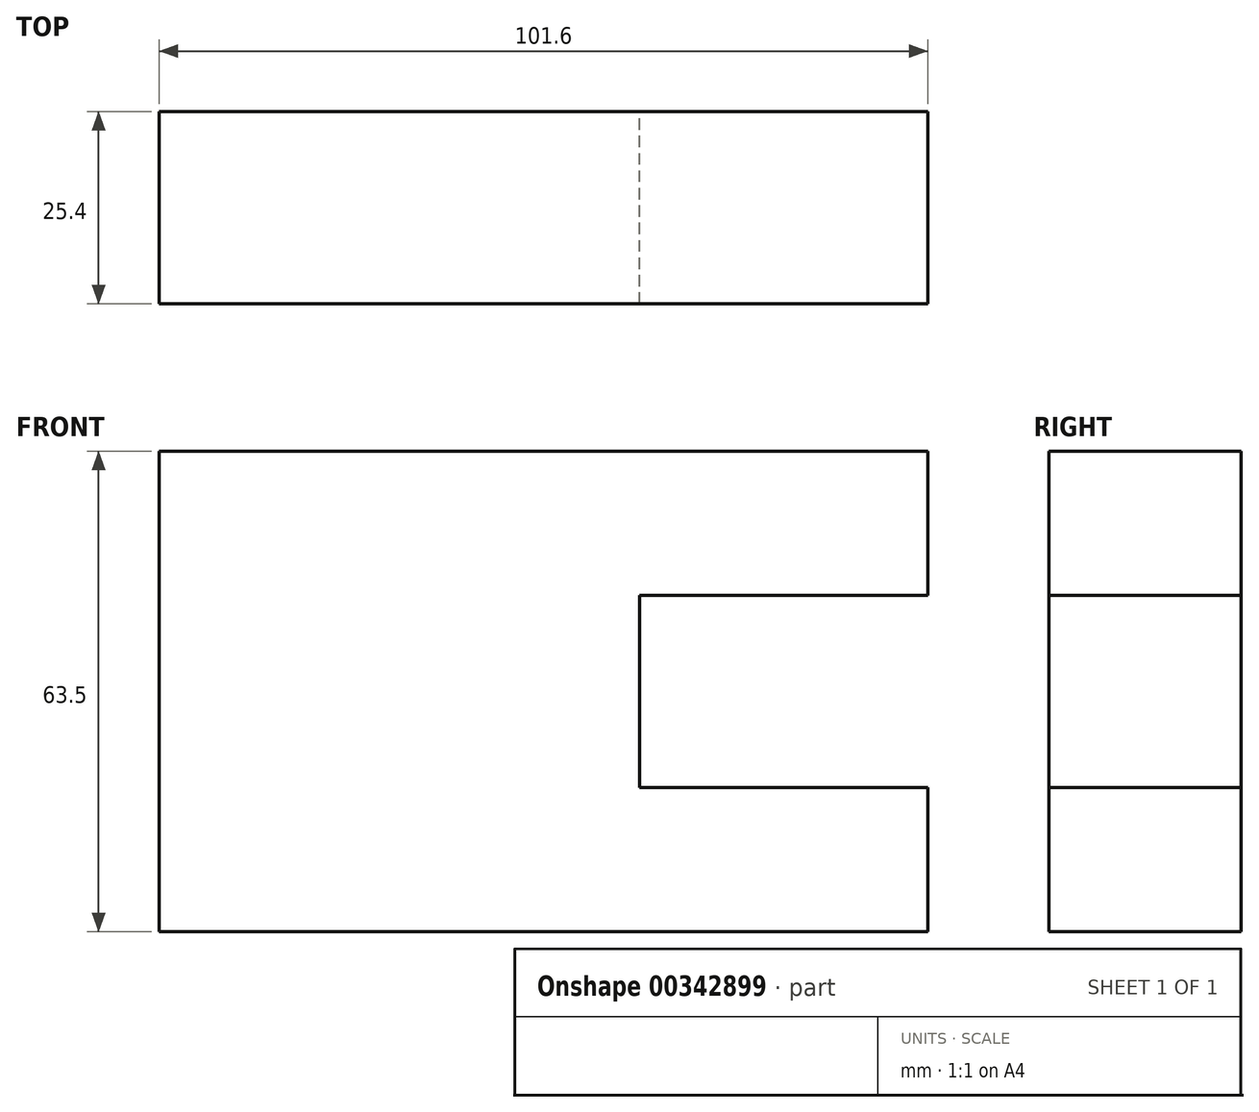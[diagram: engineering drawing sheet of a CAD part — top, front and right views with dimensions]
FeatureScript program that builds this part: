
annotation { "Feature Type Name" : "Feature", "Feature Type Description" : "" }
export const myFeature = defineFeature(function(context is Context, id is Id, definition is map)
    precondition{}
    {
        {
            var Q0;
            Q0=qCreatedBy(makeId("Front.planeOp"),FACE);
            var sketch = newSketch(context, id + "F0", { "sketchPlane" : qUnion([Q0])});
            skLineSegment(sketch, "E0", {"start": v(-65.3, 24.34) * mm, "end": v(36.3, 24.34) * mm});
            skLineSegment(sketch, "E1", {"start": v(36.3, 24.34) * mm, "end": v(36.3, 5.29) * mm});
            skLineSegment(sketch, "E2", {"start": v(36.3, 5.29) * mm, "end": v(-1.8, 5.29) * mm});
            skLineSegment(sketch, "E3", {"start": v(-1.8, 5.29) * mm, "end": v(-1.8, -20.11) * mm});
            skLineSegment(sketch, "E4", {"start": v(-1.8, -20.11) * mm, "end": v(36.3, -20.11) * mm});
            skLineSegment(sketch, "E5", {"start": v(36.3, -20.11) * mm, "end": v(36.3, -39.16) * mm});
            skLineSegment(sketch, "E6", {"start": v(36.3, -39.16) * mm, "end": v(-65.3, -39.16) * mm});
            skLineSegment(sketch, "E7", {"start": v(-65.3, -39.16) * mm, "end": v(-65.3, 24.34) * mm});
            skSolve(sketch);
        }
        {
            var Q0;
            Q0=makeQuery(id+"F0.imprint","IMPRINT",FACE,{"disambiguationData":[TD([[makeQuery(id+"F0.imprint","IMPRINT",EDGE,{"derivedFrom":sQuery(id+"F0.wireOp",EDGE,"E0")}),-1.0]])]});
            extrude(context, id + "F1", {"entities" : qUnion([Q0]), "depth" : 25.4 * mm});
        }
    });
